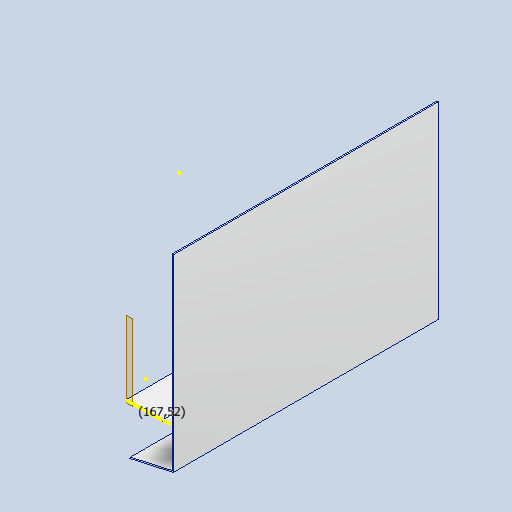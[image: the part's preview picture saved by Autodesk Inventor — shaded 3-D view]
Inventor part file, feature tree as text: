
AUTODESK INVENTOR PART (.ipt)
format: ipt  version: 2023 (Build 270158000, 158)  size: 152,064 bytes
history: native  units: mm
features: reference x15, other x6, sketch x3, extrude x2, projected_geometry x2, plane x1
ambient origin geometry x8: Origin, YZ Plane, XZ Plane, XY Plane, X Axis, Y Axis, Z Axis, Center Point
bodies: Solid1 (feature_tree)
feature tree (29):
  extrude  "Extrusion1"  Depth=0.5mm
  plane  "Work Plane1"
  extrude  "Extrusion2"  Depth=0.5mm
  sketch  "Sketch3"  dims[d6=100.0mm d7=0.0mm d8=0.5mm d9=60.0mm d10=0.0mm d11=29.238253mm]
  sketch  "Sketch1"  dims[d0=0.5mm d1=0.5mm]
  reference  "Reference1"
  reference  "Reference2"
  reference  "Reference3"
  reference  "Reference4"
  reference  "Reference5"
  reference  "Reference6"
  reference  "Reference7"
  reference  "Reference8"
  reference  "Reference9"
  reference  "Reference10"
  reference  "Reference11"
  sketch  "Sketch2"  dims[d4=0.5mm d5=0.5mm]
  reference  "Reference12"
  reference  "Reference13"
  reference  "Reference14"
  reference  "Reference15"
  projected_geometry  "Projected Loop1"
  projected_geometry  "Projected Loop2"
  other  "Assembly2"
  other  "pług:1"
  other  "sciana_lewa_v3:1"
  other  "minisumopodsr:1"
  other  "uchwytlewy:1"
  other  "uchwytprawy:1"
